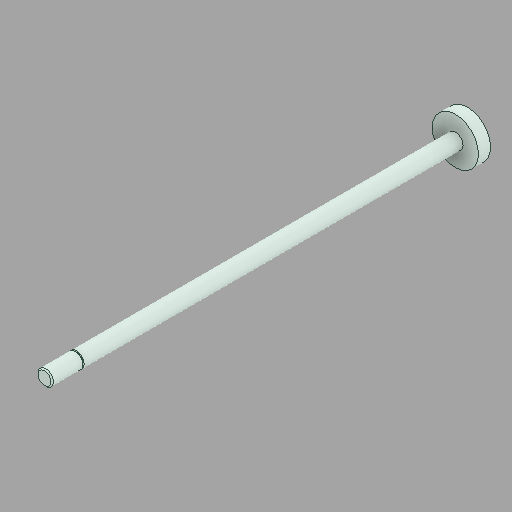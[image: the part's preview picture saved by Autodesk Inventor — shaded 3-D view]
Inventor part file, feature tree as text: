
AUTODESK INVENTOR PART (.ipt)
format: ipt  version: 2024.2 (Build 282272000, 272)  size: 90,112 bytes
history: native  units: in
note: dims shown in document units (in); Inventor stores cm internally (conversion verified against a paired STEP export)
features: thread x1
ambient origin geometry x8: Origin, YZ Plane, XZ Plane, XY Plane, X Axis, Y Axis, Z Axis, Center Point
bodies: Solid1 (feature_tree)
feature tree (1):
  thread  "Threads"  [1 undecoded]
note: 1 required parameter value undecoded (feature->parameter linkage not recoverable at this tier; creation-order binding heuristic only, values carry confidence <= 0.55)
